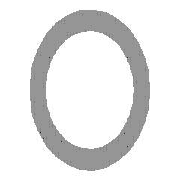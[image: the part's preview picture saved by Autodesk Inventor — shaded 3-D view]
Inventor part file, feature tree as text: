
AUTODESK INVENTOR PART (.ipt)
format: ipt  version: 2013 (Build 170138000, 138)  size: 114,176 bytes
history: native  units: mm (DEFAULTED — no unit token found)
features: other x4, sketch x3, plane x1
ambient origin geometry x8: Origin, YZ Plane, XZ Plane, XY Plane, X Axis, Y Axis, Z Axis, Center Point
bodies: Solid1 (feature_tree), Body (feature_tree)
feature tree (8):
  parser-record x1  (decoder bookkeeping rows leaked as tree rows — omitted from the tree; the rows remain in map.json)
  other  "Driven Length"
  other  "Start plane"
  other  "End plane"
  sketch  "Sketch"  dims[d2=63.5mm d3=0.0mm d4=-0.0mm d5=63.5mm d6=90.0deg d7=63.5mm]
  sketch  "Sketch3"  dims[d0=42.164mm]
  plane  "Work Plane3"
  sketch  "Sketch4"  dims[d1=3.556mm]
